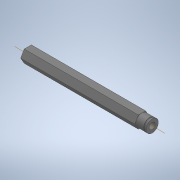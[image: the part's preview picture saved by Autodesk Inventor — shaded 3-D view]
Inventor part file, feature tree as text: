
AUTODESK INVENTOR PART (.ipt)
format: ipt  version: 2020 (Build 240168000, 168)  size: 127,488 bytes
history: native  units: in
note: dims shown in document units (in); Inventor stores cm internally (conversion verified against a paired STEP export)
features: sketch x2, extrude x1, hole x1, projected_geometry x1, other x1
ambient origin geometry x8: Origin, YZ Plane, XZ Plane, XY Plane, X Axis, Y Axis, Z Axis, Center Point
bodies: Solid1 (feature_tree)
feature tree (6):
  extrude  "Extrusion1"  [1 undecoded]
  hole  "Hole1"  [1 undecoded]
  sketch  "Sketch1"  dims[d0=2.4in d1=0.0in]
  projected_geometry  "Projected Loop1"
  sketch  "Sketch2"  dims[d2=0.196in d3=0.5in d4=0.375in d5=0.25in d6=0.5635in d7=1.0in d8=0.8108in]
  other  "Cut-Extrude1"
note: 2 required parameter values undecoded (feature->parameter linkage not recoverable at this tier; creation-order binding heuristic only, values carry confidence <= 0.55)
